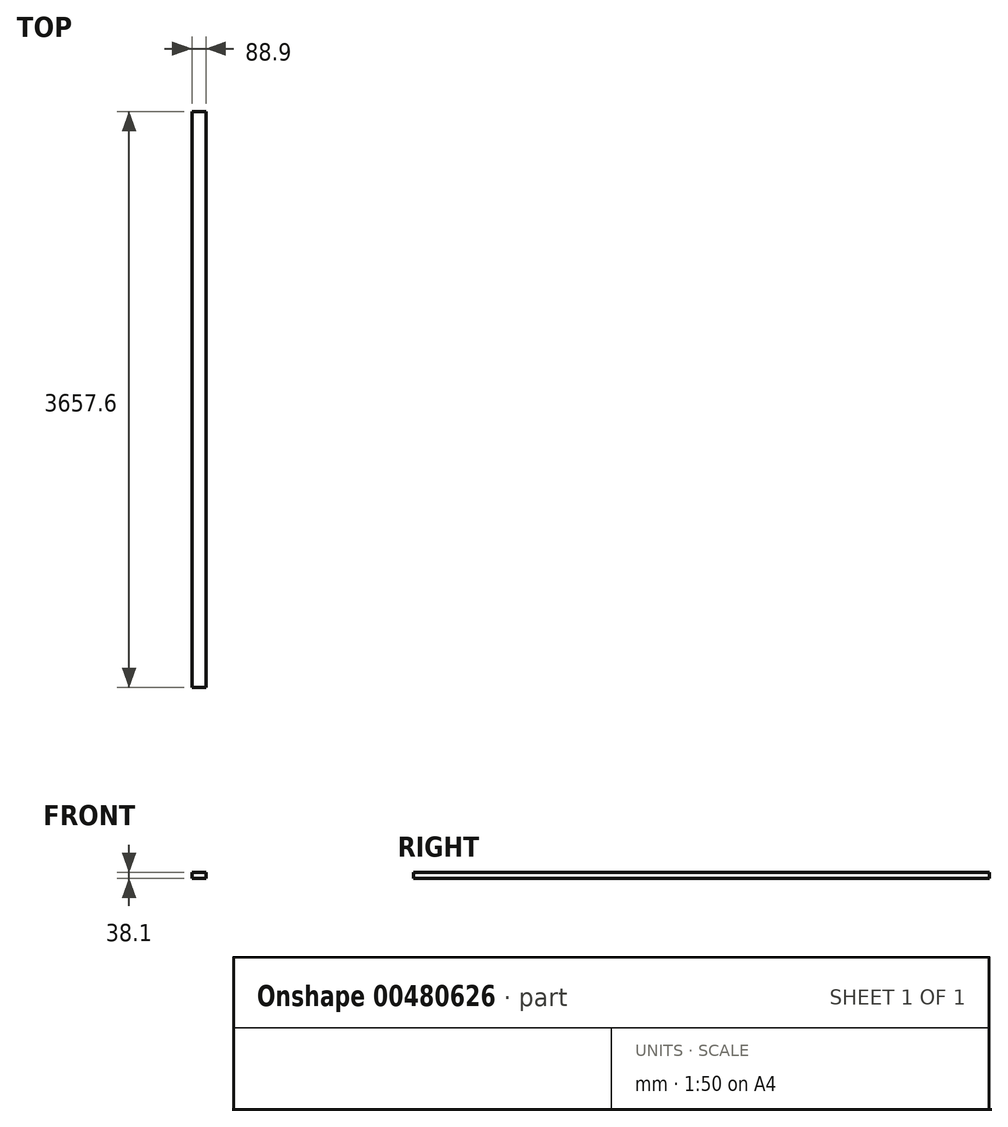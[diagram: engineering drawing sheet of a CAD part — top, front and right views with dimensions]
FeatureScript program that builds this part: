
annotation { "Feature Type Name" : "Feature", "Feature Type Description" : "" }
export const myFeature = defineFeature(function(context is Context, id is Id, definition is map)
    precondition{}
    {
        {
            var Q0;
            Q0=qCreatedBy(makeId("Front.planeOp"),FACE);
            var sketch = newSketch(context, id + "F0", { "sketchPlane" : qUnion([Q0])});
            skLineSegment(sketch, "E0.bottom", {"start": v(0, 0) * mm, "end": v(88.9, 0) * mm});
            skLineSegment(sketch, "E0.top", {"start": v(0, 38.1) * mm, "end": v(88.9, 38.1) * mm});
            skLineSegment(sketch, "E0.left", {"start": v(0, 0) * mm, "end": v(0, 38.1) * mm});
            skLineSegment(sketch, "E0.right", {"start": v(88.9, 0) * mm, "end": v(88.9, 38.1) * mm});
            skSolve(sketch);
        }
        {
            var Q0;
            Q0=makeQuery(id+"F0.imprint","IMPRINT",FACE,{"disambiguationData":[TD([[makeQuery(id+"F0.imprint","IMPRINT",EDGE,{"derivedFrom":sQuery(id+"F0.wireOp",EDGE,"E0.bottom")}),1.0]])]});
            extrude(context, id + "F1", {"entities" : qUnion([Q0]), "endBound" : BoundingType.SYMMETRIC, "depth" : 3657.6 * mm});
        }
    });
